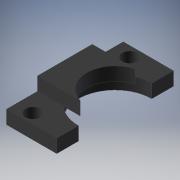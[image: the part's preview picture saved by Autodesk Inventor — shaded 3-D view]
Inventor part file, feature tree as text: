
AUTODESK INVENTOR PART (.ipt)
format: ipt  version: 2019.4 (Build 234330000, 330)  size: 149,504 bytes
history: native  units: mm
features: extrude x4, sketch x3
ambient origin geometry x8: Origin, YZ Plane, XZ Plane, XY Plane, X Axis, Y Axis, Z Axis, Center Point
bodies: Solid1 (feature_tree)
feature tree (7):
  extrude  "Extrusion1"  Depth=7.528mm
  extrude  "Extrusion2"  Depth=4.0mm
  sketch  "Sketch4"  dims[d13=0.0mm d14=8.75mm d15=2.0mm d16=0.0mm d17=4.65mm d18=4.65mm d19=2.0mm d20=0.0mm d21=2.0mm d22=0.0mm d23=0.0mm]
  extrude  "Extrusion3"  Depth=2.0mm
  extrude  "Extrusion4"  Depth=2.0mm TaperAngle=0.0deg
  sketch  "Sketch1"  dims[d0=17.5mm d1=2.5mm d2=2.5mm d3=1.5mm d4=1.5mm d5=2.3mm d6=2.3mm d7=8.5mm d8=7.528mm d9=8.75mm]
  sketch  "Sketch3"  dims[d10=4.0mm d11=0.0mm d12=11.0mm]
